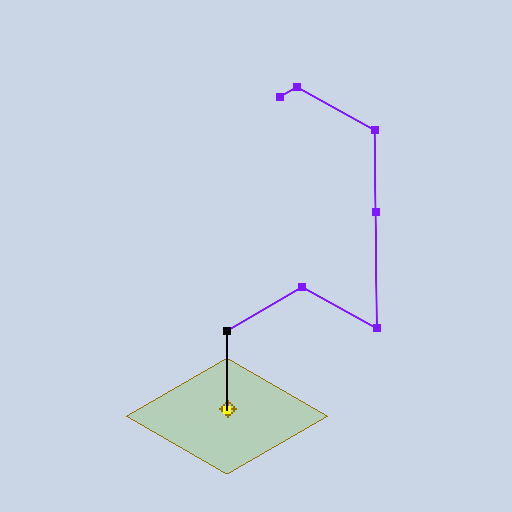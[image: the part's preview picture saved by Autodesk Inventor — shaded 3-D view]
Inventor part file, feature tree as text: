
AUTODESK INVENTOR PART (.ipt)
format: ipt  version: 2025 (Build 290162000, 162)  size: 107,520 bytes
history: native  units: in
note: dims shown in document units (in); Inventor stores cm internally (conversion verified against a paired STEP export)
features: other x1, plane x1, sketch x1
ambient origin geometry x8: Origin, YZ Plane, XZ Plane, XY Plane, X Axis, Y Axis, Z Axis, Center Point
feature tree (3):
  other  "Work Point1"
  plane  "Work Plane1"
  sketch  "3D Sketch1"
